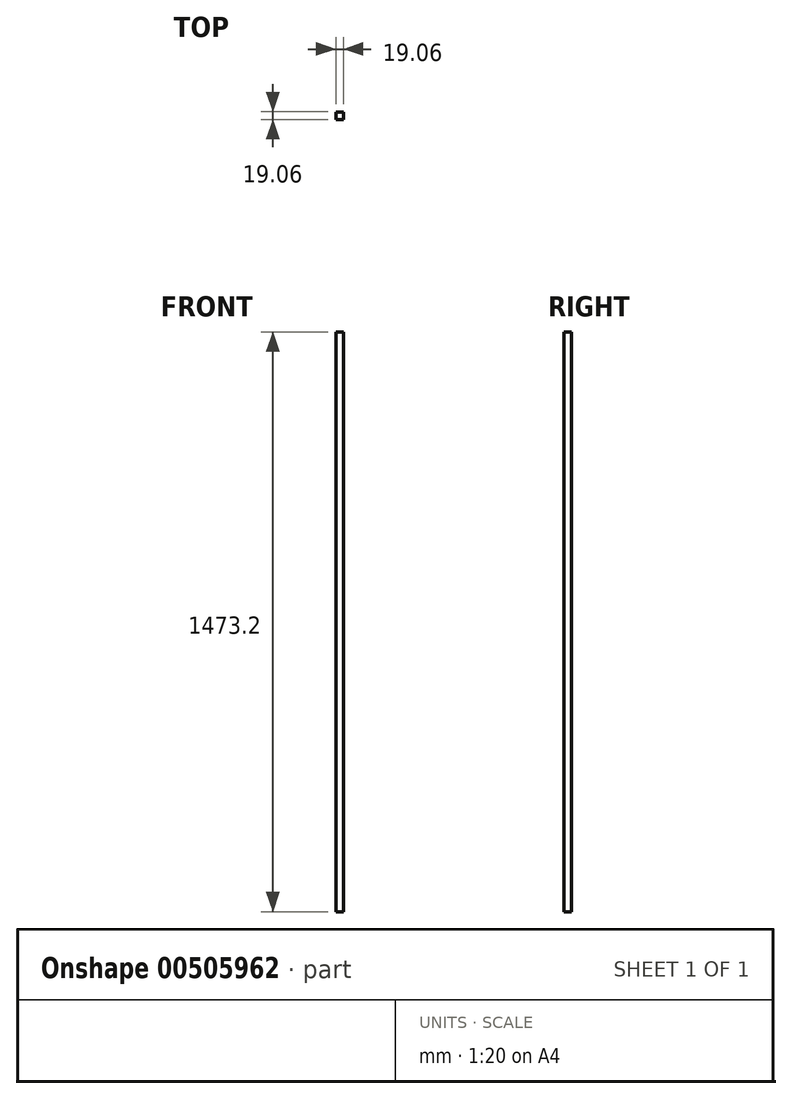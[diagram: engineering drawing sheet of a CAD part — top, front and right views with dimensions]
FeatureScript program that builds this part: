
annotation { "Feature Type Name" : "Feature", "Feature Type Description" : "" }
export const myFeature = defineFeature(function(context is Context, id is Id, definition is map)
    precondition{}
    {
        {
            var Q0;
            Q0=qCreatedBy(makeId("Top.planeOp"),FACE);
            var sketch = newSketch(context, id + "F0", { "sketchPlane" : qUnion([Q0])});
            skLineSegment(sketch, "E0.bottom", {"start": v(-9.53, 9.53) * mm, "end": v(9.53, 9.53) * mm});
            skLineSegment(sketch, "E0.top", {"start": v(-9.53, -9.53) * mm, "end": v(9.52, -9.53) * mm});
            skLineSegment(sketch, "E0.left", {"start": v(-9.53, 9.53) * mm, "end": v(-9.53, -9.53) * mm});
            skLineSegment(sketch, "E0.right", {"start": v(9.53, 9.53) * mm, "end": v(9.52, -9.53) * mm});
            skPoint(sketch, "E0.middle", {"position": v(0, 0) * mm});
            skSolve(sketch);
        }
        {
            var Q0;
            Q0=qSketchRegion(id+"F0",true);
            extrude(context, id + "F1", {"entities" : qUnion([Q0]), "depth" : 1473.2 * mm});
        }
    });
